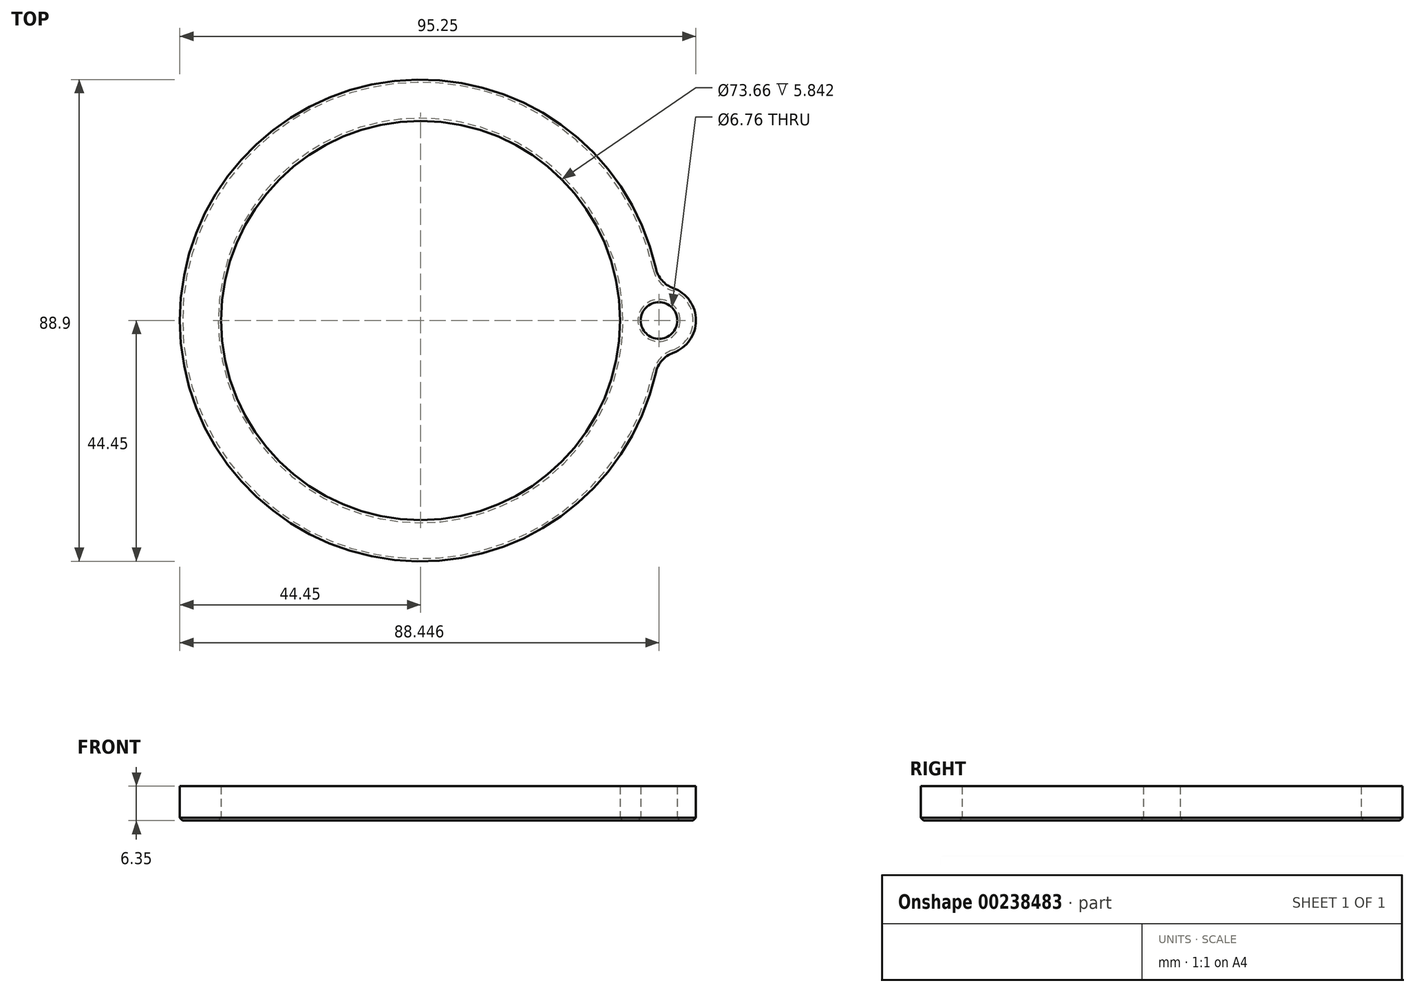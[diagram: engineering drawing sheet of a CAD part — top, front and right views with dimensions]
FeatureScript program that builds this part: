
annotation { "Feature Type Name" : "Feature", "Feature Type Description" : "" }
export const myFeature = defineFeature(function(context is Context, id is Id, definition is map)
    precondition{}
    {
        {
            var Q0;
            Q0=qCreatedBy(makeId("Top.planeOp"),FACE);
            var sketch = newSketch(context, id + "F0", { "sketchPlane" : qUnion([Q0])});
            skCircle(sketch, "E0", {"center": v(0, 0) * mm, "radius": 36.83 * mm});
            skCircle(sketch, "E1", {"center": v(0, 0) * mm, "radius": 44.45 * mm});
            skSolve(sketch);
        }
        {
            var Q0;
            Q0 = qSketchRegion(id + "F0", true);
            extrude(context, id + "F1", {"entities" : qUnion([Q0]), "depth" : 6.35 * mm});
        }
        {
            var Q0;
            Q0=makeQuery(id+"F1.opExtrude","CAP_FACE",FACE,{"disambiguationData":[OSD([sQuery(id+"F0.wireOp",EDGE,"E0"),sQuery(id+"F0.wireOp",EDGE,"E1")])],"isStart":false});
            var sketch = newSketch(context, id + "F2", { "sketchPlane" : qUnion([Q0])});
            skCircle(sketch, "E2", {"center": v(44.45, 0) * mm, "radius": 6.35 * mm});
            skSolve(sketch);
        }
        {
            var Q0;
            Q0 = qSketchRegion(id + "F2", true);
            extrude(context, id + "F3", {"entities" : qUnion([Q0]), "operationType" : NewBodyOperationType.ADD, "oppositeDirection" : true, "depth" : 6.35 * mm});
        }
        {
            var Q0;
            Q0=makeQuery(id+"F3.boolean.opBoolean","MERGE",FACE,{"derivedFrom":[makeQuery(id+"F1.opExtrude","CAP_FACE",FACE,{"disambiguationData":[OSD([sQuery(id+"F0.wireOp",EDGE,"E0"),sQuery(id+"F0.wireOp",EDGE,"E1")])],"isStart":true}),makeQuery(id+"F3.opExtrude","CAP_FACE",FACE,{"disambiguationData":[OSD([sQuery(id+"F2.wireOp",EDGE,"E2")])],"isStart":false})]});
            var sketch = newSketch(context, id + "F4", { "sketchPlane" : qUnion([Q0])});
            skPoint(sketch, "E3", {"position": v(44, 0) * mm});
            skSolve(sketch);
        }
        {
            var Q0;
            Q0=sQuery(id+"F4.wireOp",VERTEX,"E3");
            var Q1;
            Q1=makeQuery(id+"F1.opExtrude","SWEPT_BODY",BODY,{"disambiguationData":[OSD([sQuery(id+"F0.wireOp",EDGE,"E0"),sQuery(id+"F0.wireOp",EDGE,"E1")])]});
            hole(context, id + "F5", {"style" : HoleStyle.SIMPLE, "endStyle" : HoleEndStyle.BLIND, "standardTappedOrClearance" : lookupTablePath({ "standard" : "ANSI", "fit" : "Normal (ASME)", "size" : "1/4", "type" : "Clearance" }), "standardBlindInLast" : lookupTablePath({ "fit" : "Free", "standard" : "ANSI", "size" : "1/4", "type" : "Clearance" }), "holeDiameter" : 6.76 * mm, "holeDepth" : 12.7 * mm, "isTappedThrough" : true, "tappedDepth" : 12.7 * mm, "tapClearance" : 3, "locations" : qUnion([Q0]), "scope" : qUnion([Q1])});
        }
        {
            var Q0;
            Q0=qCreatedBy(makeId("Front.planeOp"),FACE);
            var sketch = newSketch(context, id + "F6", { "sketchPlane" : qUnion([Q0])});
            skLineSegment(sketch, "E4", {"start": v(0, 44.4) * mm, "end": v(0, -37.24) * mm, "construction": true});
            skSolve(sketch);
        }
        {
            var Q0;
            Q0=makeQuery(id+"F3.boolean.opBoolean","INTERSECT",EDGE,{"disambiguationData":[OD(1.0)],"derivedFrom":[makeQuery(id+"F1.opExtrude","SWEPT_FACE",FACE,{"disambiguationData":[OSD([sQuery(id+"F0.wireOp",EDGE,"E1")])]}),makeQuery(id+"F3.opExtrude","SWEPT_FACE",FACE,{"disambiguationData":[OSD([sQuery(id+"F2.wireOp",EDGE,"E2")])]})]});
            var Q1;
            Q1=makeQuery(id+"F3.boolean.opBoolean","INTERSECT",EDGE,{"disambiguationData":[OD(0.0)],"derivedFrom":[makeQuery(id+"F1.opExtrude","SWEPT_FACE",FACE,{"disambiguationData":[OSD([sQuery(id+"F0.wireOp",EDGE,"E1")])]}),makeQuery(id+"F3.opExtrude","SWEPT_FACE",FACE,{"disambiguationData":[OSD([sQuery(id+"F2.wireOp",EDGE,"E2")])]})]});
            fillet(context, id + "F7", {"entities" : qUnion([Q0, Q1]), "radius" : 5.08 * mm, "tangentPropagation" : true, "allowEdgeOverflow" : false});
        }
        {
            var Q0;
            {var subQ0=sQuery(id+"F2.wireOp",EDGE,"E2");Q0=makeQuery(id+"FZmdLmcNQyuIU38_1.5.F3.boolean.opBoolean","MERGE",FACE,{"derivedFrom":[makeQuery(id+"FZmdLmcNQyuIU38_1.4.F3.boolean.opBoolean","MERGE",FACE,{"derivedFrom":[makeQuery(id+"FZmdLmcNQyuIU38_1.3.F3.boolean.opBoolean","MERGE",FACE,{"derivedFrom":[makeQuery(id+"FZmdLmcNQyuIU38_1.2.F3.boolean.opBoolean","MERGE",FACE,{"derivedFrom":[makeQuery(id+"FZmdLmcNQyuIU38_1.1.F3.boolean.opBoolean","MERGE",FACE,{"derivedFrom":[makeQuery(id+"F3.boolean.opBoolean","MERGE",FACE,{"derivedFrom":[makeQuery(id+"F1.opExtrude","CAP_FACE",FACE,{"disambiguationData":[OSD([sQuery(id+"F0.wireOp",EDGE,"E0"),sQuery(id+"F0.wireOp",EDGE,"E1")])],"isStart":true}),makeQuery(id+"F3.opExtrude","CAP_FACE",FACE,{"disambiguationData":[OSD([subQ0])],"isStart":false})]}),makeQuery(id+"FZmdLmcNQyuIU38_1.1.F3.opExtrude","CAP_FACE",FACE,{"disambiguationData":[OSD([subQ0])],"isStart":false})]}),makeQuery(id+"FZmdLmcNQyuIU38_1.2.F3.opExtrude","CAP_FACE",FACE,{"disambiguationData":[OSD([subQ0])],"isStart":false})]}),makeQuery(id+"FZmdLmcNQyuIU38_1.3.F3.opExtrude","CAP_FACE",FACE,{"disambiguationData":[OSD([subQ0])],"isStart":false})]}),makeQuery(id+"FZmdLmcNQyuIU38_1.4.F3.opExtrude","CAP_FACE",FACE,{"disambiguationData":[OSD([subQ0])],"isStart":false})]}),makeQuery(id+"FZmdLmcNQyuIU38_1.5.F3.opExtrude","CAP_FACE",FACE,{"disambiguationData":[OSD([subQ0])],"isStart":false})]});}
            chamfer(context, id + "F8", {"entities" : qUnion([Q0]), "width" : 0.5 * mm, "tangentPropagation" : true});
        }
    });
